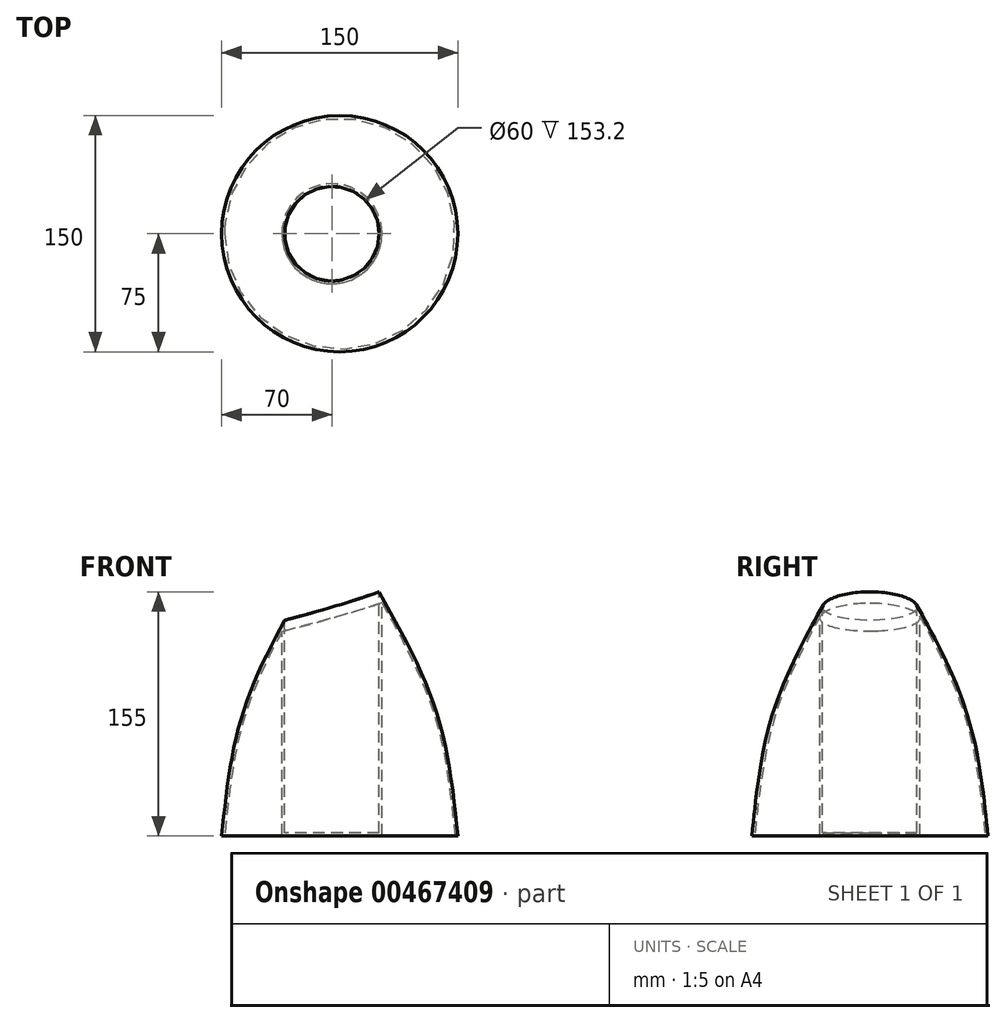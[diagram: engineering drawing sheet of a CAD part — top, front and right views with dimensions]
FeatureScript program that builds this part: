
annotation { "Feature Type Name" : "Feature", "Feature Type Description" : "" }
export const myFeature = defineFeature(function(context is Context, id is Id, definition is map)
    precondition{}
    {
        {
            var Q0;
            Q0=qCreatedBy(makeId("Top.planeOp"),FACE);
            var sketch = newSketch(context, id + "F0", { "sketchPlane" : qUnion([Q0])});
            skCircle(sketch, "E0", {"center": v(0, 0) * mm, "radius": 75 * mm});
            skSolve(sketch);
        }
        {
            var Q0;
            Q0=qCreatedBy(makeId("Top.planeOp"),FACE);
            cPlane(context, id + "F1", {"entities" : qUnion([Q0]), "cplaneType" : CPlaneType.OFFSET, "offset" : 75 * mm, "width" : 150 * mm, "height" : 150 * mm});
        }
        {
            var Q0;
            Q0=qCreatedBy(id+"F1.planeOp",FACE);
            var sketch = newSketch(context, id + "F2", { "sketchPlane" : qUnion([Q0])});
            skCircle(sketch, "E1", {"center": v(0, 0) * mm, "radius": 62.5 * mm});
            skSolve(sketch);
        }
        {
            var Q0;
            Q0=qCreatedBy(id+"F1.planeOp",FACE);
            cPlane(context, id + "F3", {"entities" : qUnion([Q0]), "cplaneType" : CPlaneType.OFFSET, "offset" : 80 * mm, "width" : 150 * mm, "height" : 150 * mm});
        }
        {
            var Q0;
            Q0=qCreatedBy(id+"F3.planeOp",FACE);
            var sketch = newSketch(context, id + "F4", { "sketchPlane" : qUnion([Q0])});
            skCircle(sketch, "E2", {"center": v(0, 0) * mm, "radius": 25 * mm});
            skSolve(sketch);
        }
        {
            var Q0;
            Q0=makeQuery(id+"F0.imprint","IMPRINT",FACE,{"disambiguationData":[TD([[makeQuery(id+"F0.imprint","IMPRINT",EDGE,{"derivedFrom":sQuery(id+"F0.wireOp",EDGE,"E0")}),1.0]])]});
            var Q1;
            Q1=makeQuery(id+"F2.imprint","IMPRINT",FACE,{"disambiguationData":[TD([[makeQuery(id+"F2.imprint","IMPRINT",EDGE,{"derivedFrom":sQuery(id+"F2.wireOp",EDGE,"E1")}),1.0]])]});
            var Q2;
            Q2=makeQuery(id+"F4.imprint","IMPRINT",FACE,{"disambiguationData":[TD([[makeQuery(id+"F4.imprint","IMPRINT",EDGE,{"derivedFrom":sQuery(id+"F4.wireOp",EDGE,"E2")}),1.0]])]});
            loft(context, id + "F5", {"sheetProfilesArray" : [{ "sheetProfileEntities" : qUnion([Q0]) }, { "sheetProfileEntities" : qUnion([Q1]) }, { "sheetProfileEntities" : qUnion([Q2]) }]});
        }
        {
            var Q0;
            Q0=qCreatedBy(id+"F3.planeOp",FACE);
            var sketch = newSketch(context, id + "F6", { "sketchPlane" : qUnion([Q0])});
            skLineSegment(sketch, "E3", {"start": v(0, 0) * mm, "end": v(-5, 0) * mm});
            skCircle(sketch, "E4", {"center": v(-5, 0) * mm, "radius": 30 * mm});
            skSolve(sketch);
        }
        {
            var Q0;
            Q0=makeQuery(id+"F6.imprint","IMPRINT",FACE,{"disambiguationData":[TD([[makeQuery(id+"F6.imprint","IMPRINT",EDGE,{"derivedFrom":sQuery(id+"F6.wireOp",EDGE,"E4")}),1.0]])]});
            var Q1;
            Q1=sQuery(id+"F6.wireOp",EDGE,"E4");
            extrude(context, id + "F7", {"entities" : qUnion([Q0]), "operationType" : NewBodyOperationType.REMOVE, "surfaceEntities" : qUnion([Q1]), "oppositeDirection" : true, "depth" : 153.2 * mm});
        }
        {
            var Q0;
            Q0=makeQuery(id+"F5.opLoft","CAP_FACE",FACE,{"disambiguationData":[OSD([makeQuery(id+"F0.imprint","IMPRINT",FACE,{"disambiguationData":[TD([[makeQuery(id+"F0.imprint","IMPRINT",EDGE,{"derivedFrom":sQuery(id+"F0.wireOp",EDGE,"E0")}),1.0]])]})])],"isStart":true});
            shell(context, id + "F8", {"entities" : qUnion([Q0]), "thickness" : 1.8 * mm});
        }
    });
